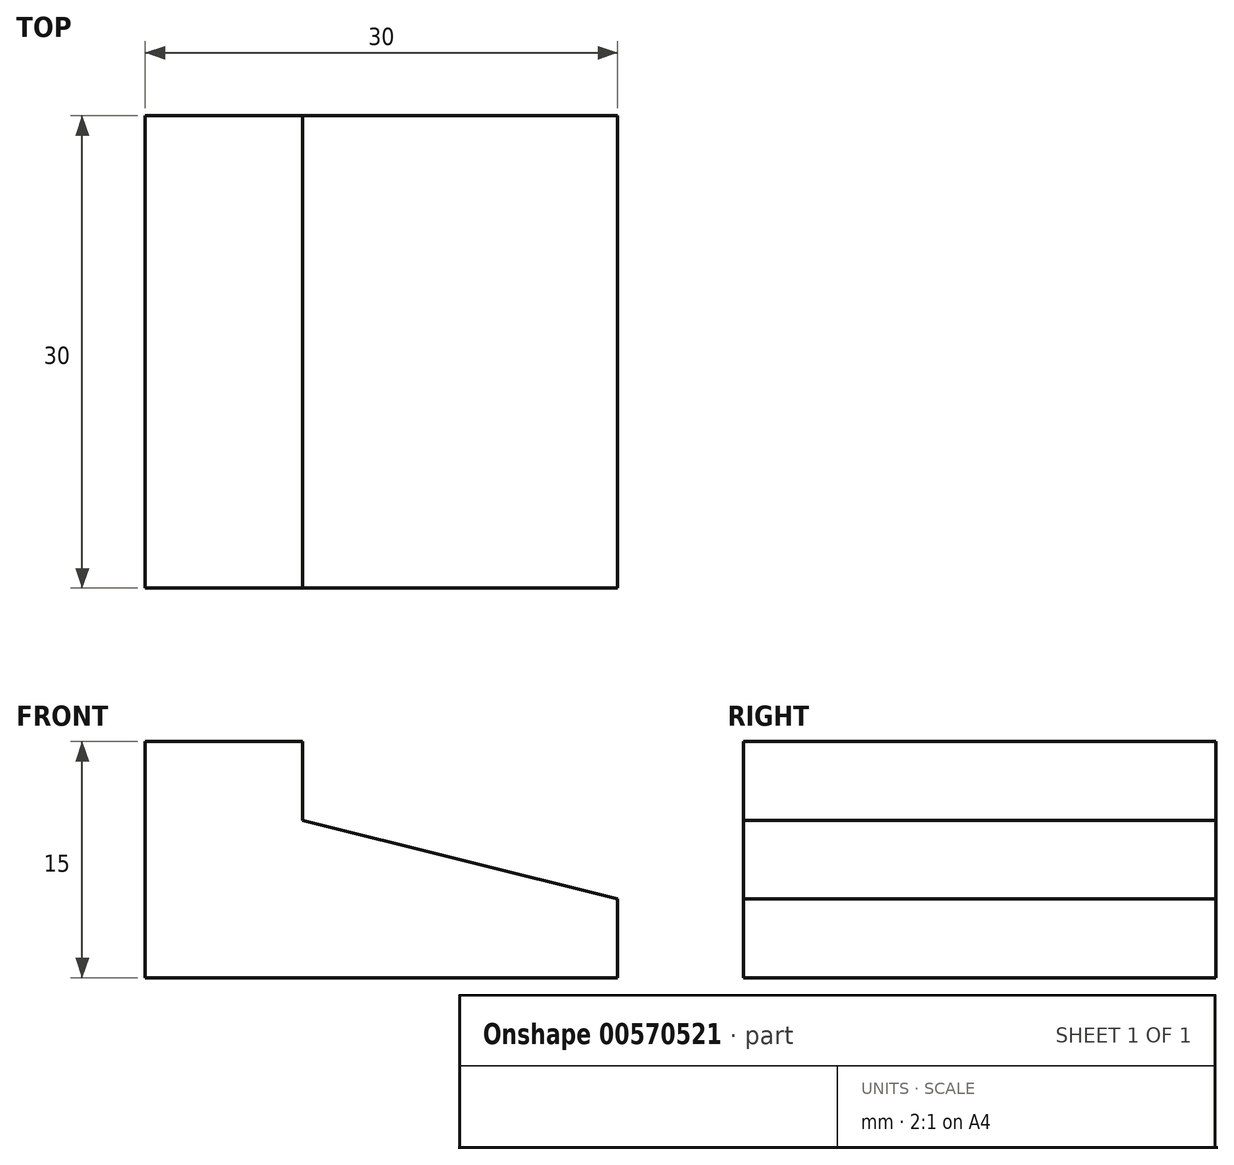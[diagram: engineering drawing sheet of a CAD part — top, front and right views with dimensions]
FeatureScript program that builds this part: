
annotation { "Feature Type Name" : "Feature", "Feature Type Description" : "" }
export const myFeature = defineFeature(function(context is Context, id is Id, definition is map)
    precondition{}
    {
        {
            var Q0;
            Q0=qCreatedBy(makeId("Top.planeOp"),FACE);
            var sketch = newSketch(context, id + "F0", { "sketchPlane" : qUnion([Q0])});
            skLineSegment(sketch, "E0.bottom", {"start": v(-12.77, 18.15) * mm, "end": v(17.23, 18.15) * mm});
            skLineSegment(sketch, "E0.top", {"start": v(-12.77, -11.85) * mm, "end": v(17.23, -11.85) * mm});
            skLineSegment(sketch, "E0.left", {"start": v(-12.77, 18.15) * mm, "end": v(-12.77, -11.85) * mm});
            skLineSegment(sketch, "E0.right", {"start": v(17.23, 18.15) * mm, "end": v(17.23, -11.85) * mm});
            skSolve(sketch);
        }
        {
            var Q0;
            Q0=qSketchRegion(id+"F0",true);
            extrude(context, id + "F1", {"entities" : qUnion([Q0]), "depth" : 15 * mm});
        }
        {
            var Q0;
            Q0=makeQuery(id+"F1.opExtrude","SWEPT_FACE",FACE,{"disambiguationData":[OSD([sQuery(id+"F0.wireOp",EDGE,"E0.top")])]});
            var sketch = newSketch(context, id + "F2", { "sketchPlane" : qUnion([Q0])});
            skLineSegment(sketch, "E1", {"start": v(-2.77, 15) * mm, "end": v(-2.77, 10) * mm});
            skLineSegment(sketch, "E2", {"start": v(-2.77, 10) * mm, "end": v(17.23, 5) * mm});
            skLineSegment(sketch, "E3", {"start": v(17.23, 5) * mm, "end": v(17.23, 0) * mm});
            skLineSegment(sketch, "E4", {"start": v(-2.77, 15) * mm, "end": v(-12.77, 15) * mm});
            skSolve(sketch);
        }
        {
            var Q0;
            {var subQ0=sQuery(id+"F2.wireOp",EDGE,"E1");Q0=makeQuery(id+"F2.imprint","IMPRINT",FACE,{"disambiguationData":[TD([[makeQuery(id+"F2.imprint","IMPRINT",EDGE,{"derivedFrom":subQ0}),1.0]])]});}
            extrude(context, id + "F3", {"entities" : qUnion([Q0]), "operationType" : NewBodyOperationType.REMOVE, "endBound" : BoundingType.THROUGH_ALL, "oppositeDirection" : true, "depth" : 25 * mm});
        }
    });
